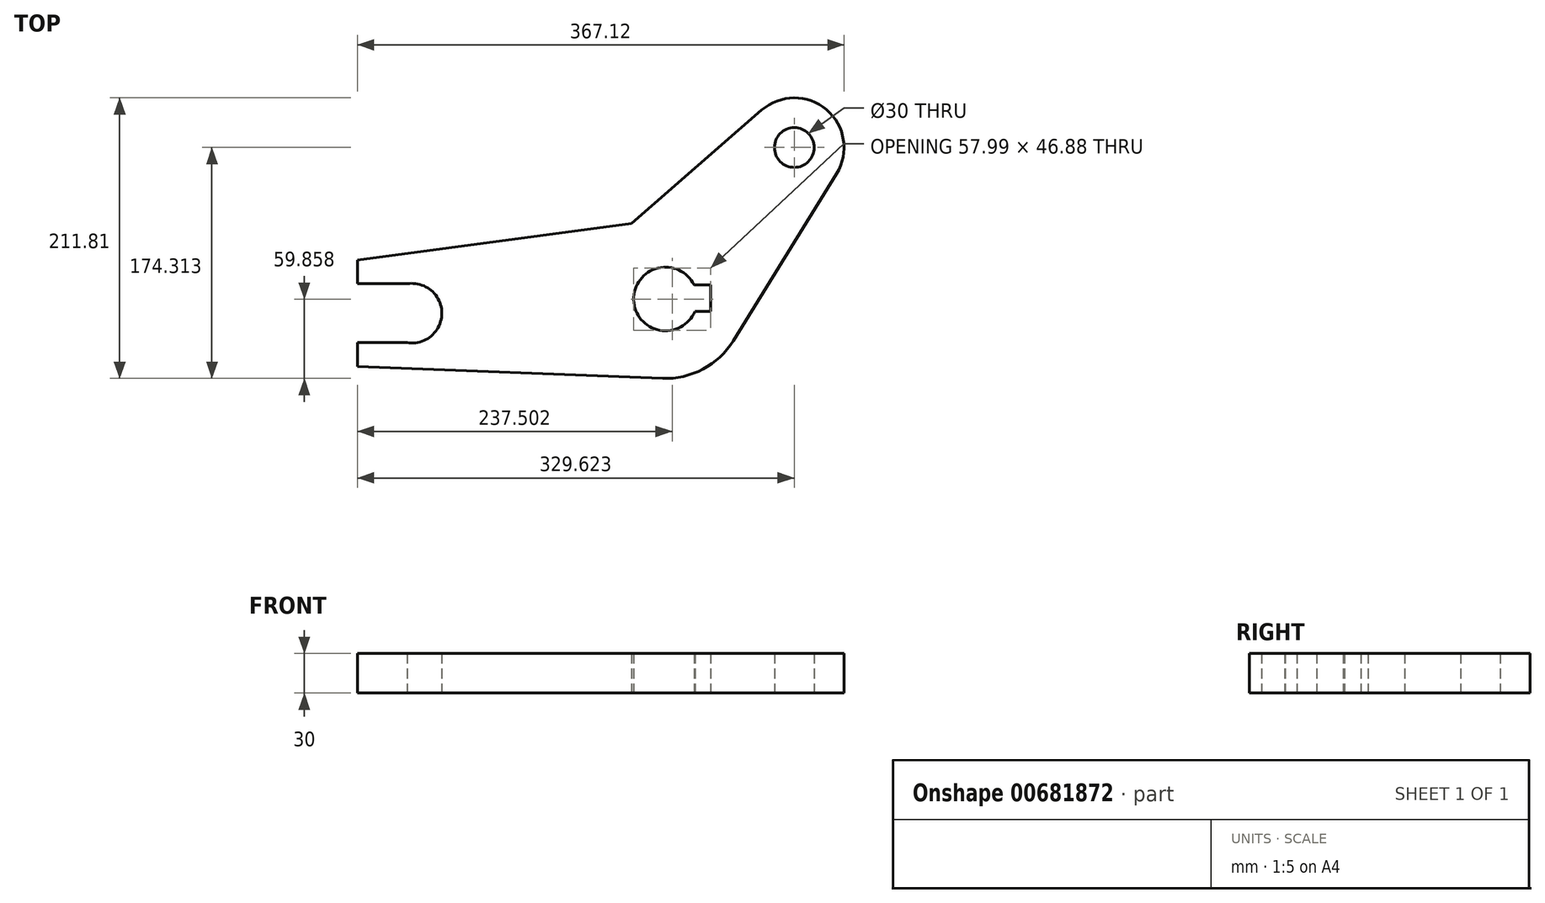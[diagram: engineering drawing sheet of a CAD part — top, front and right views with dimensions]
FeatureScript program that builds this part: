
annotation { "Feature Type Name" : "Feature", "Feature Type Description" : "" }
export const myFeature = defineFeature(function(context is Context, id is Id, definition is map)
    precondition{}
    {
        {
            var Q0;
            Q0=qCreatedBy(makeId("Top.planeOp"),FACE);
            var sketch = newSketch(context, id + "F0", { "sketchPlane" : qUnion([Q0])});
            skLineSegment(sketch, "E0", {"start": v(-50.56, 46) * mm, "end": v(-50.56, 28) * mm});
            skLineSegment(sketch, "E1", {"start": v(-50.56, -16.38) * mm, "end": v(-50.56, -34.38) * mm});
            skLineSegment(sketch, "E2", {"start": v(-50.56, 28) * mm, "end": v(-13.06, 28) * mm});
            skLineSegment(sketch, "E3", {"start": v(-50.56, -16.38) * mm, "end": v(-13.06, -16.38) * mm});
            skArc(sketch, "E4", {"start": v(-13.06, -16.38) * mm, "mid": v(13.17, 5.81) * mm, "end": v(-13.06, 28) * mm});
            skArc(sketch, "E5", {"start": v(203.46, 27.19) * mm, "mid": v(157.95, 15.88) * mm, "end": v(204.03, 7.19) * mm});
            skCircle(sketch, "E6", {"center": v(181.94, 16.56) * mm, "radius": 60 * mm});
            skLineSegment(sketch, "E7", {"start": v(-50.56, -34.38) * mm, "end": v(179.59, -43.39) * mm});
            skLineSegment(sketch, "E8", {"start": v(-50.56, 46) * mm, "end": v(173.98, 76.03) * mm});
            skCircle(sketch, "E9", {"center": v(279.06, 130.87) * mm, "radius": 15 * mm});
            skCircle(sketch, "E10", {"center": v(279.06, 130.87) * mm, "radius": 37.5 * mm});
            skLineSegment(sketch, "E11", {"start": v(203.46, 27.19) * mm, "end": v(215.94, 27.19) * mm});
            skLineSegment(sketch, "E12", {"start": v(215.94, 27.19) * mm, "end": v(215.94, 7.19) * mm});
            skLineSegment(sketch, "E13", {"start": v(215.94, 7.19) * mm, "end": v(204.03, 7.19) * mm});
            skLineSegment(sketch, "E14", {"start": v(254.45, 159.17) * mm, "end": v(142.56, 61.83) * mm});
            skLineSegment(sketch, "E15", {"start": v(232.97, -14.99) * mm, "end": v(310.96, 111.15) * mm});
            skPoint(sketch, "E16.end.orphan", {"position": v(13.17, 5.81) * mm});
            skSolve(sketch);
        }
        {
            var Q0;
            {var subQ0=sQuery(id+"F0.wireOp",EDGE,"E0");Q0=makeQuery(id+"F0.imprint","IMPRINT",FACE,{"disambiguationData":[TD([[makeQuery(id+"F0.imprint","IMPRINT",EDGE,{"derivedFrom":subQ0}),1.0]])]});}
            var Q1;
            Q1=makeQuery(id+"F0.imprint","IMPRINT",FACE,{"disambiguationData":[TD([[makeQuery(id+"F0.imprint","IMPRINT",EDGE,{"derivedFrom":sQuery(id+"F0.wireOp",EDGE,"E9")}),-1.0]])]});
            var Q2;
            {var subQ0=sQuery(id+"F0.wireOp",EDGE,"E8");var subQ1=sQuery(id+"F0.wireOp",EDGE,"E6");var subQ2=makeQuery(id+"F0.imprint","INTERSECT",VERTEX,{"derivedFrom":[subQ1,subQ0]});Q2=makeQuery(id+"F0.imprint","IMPRINT",FACE,{"disambiguationData":[TD([[makeQuery(id+"F0.imprint","IMPRINT",EDGE,{"disambiguationData":[TD([[subQ2,-1.0]])],"derivedFrom":subQ1}),-1.0]])]});}
            var Q3;
            Q3=makeQuery(id+"F0.imprint","IMPRINT",FACE,{"disambiguationData":[TD([[makeQuery(id+"F0.imprint","IMPRINT",EDGE,{"derivedFrom":sQuery(id+"F0.wireOp",EDGE,"E5")}),-1.0]])]});
            var Q4;
            {var subQ7=sQuery(id+"F0.wireOp",EDGE,"E15");Q4=makeQuery(id+"F0.imprint","IMPRINT",FACE,{"disambiguationData":[TD([[makeQuery(id+"F0.imprint","IMPRINT",EDGE,{"derivedFrom":subQ7}),1.0]])]});}
            extrude(context, id + "F1", {"entities" : qUnion([Q0, Q1, Q2, Q3, Q4]), "depth" : 30 * mm, "offsetDistance" : 25 * mm});
        }
    });
